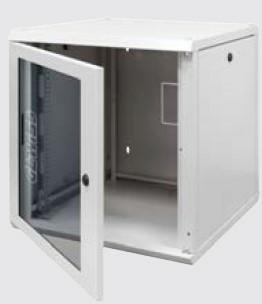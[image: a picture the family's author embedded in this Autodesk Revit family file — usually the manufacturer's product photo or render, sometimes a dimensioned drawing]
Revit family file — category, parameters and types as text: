
# Revit family: Domotics-CablaggioStrutturato-GEWISS-QUADRI_PARETE_19_12U_P400
name_source: partatom
category: Apparecchi elettrici
units: mm (PartAtom-declared; Revit-internal decimal feet)

## family parameters
Condiviso = No
Host = Superficie
Mantenere orientamento annotazione = Sì
Punto di calcolo locali = Sì
Quota connettore circolare = Usa diametro
Taglio con vuoti quando caricato = No
Tipo di parte = Normale

## types (1)
- Domotics-CablaggioStrutturato-GEWISS-QUADRI_PARETE_19_12U_P400
    Apertura porta = 180°
    Catalogo = DOMOTICS
    Categoria = Quadro da parete 19"
    Codice Electrocod = 3752
    Colore = Grigio (RAL 7035)
    Descrizione = QUADRO DA PARETE 19 12U P=400MM.
    Dim. esterne BxHxP (mm) = 600x605x400
    Finitura = Bucciata
    Grado di protezione = IP20
    IDF = 31048a0f-3bf5-46e9-84e3-9b2dc10e415f
    IDT = 601a335b6a224bb6a86d85924b08be06
    Immagine tipo = B.jpg
    Materiale = Acciaio
    Modello = GW38408
    N. montanti = 2
    N_poli = 1
    Portata statica = 50KG
    Potenza quadro = 0 V
    Produttore = GEWISS S.p.A.
    Profondità (mm) = 400 mm
    Prospetto di default = 1219 mm
    SEO = Quadro
    Scheda Tecnica = https://www.gewiss.com
    Tipologia porta = Reversibile
    URL = https://www.gewiss.com
    Unità di cablaggio = 12 U
    Versione file RFA = 21.2

## geometry (parser evidence)
native form markers: Sweep x4
no freeform markers — native parametric forms only
